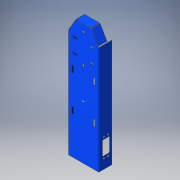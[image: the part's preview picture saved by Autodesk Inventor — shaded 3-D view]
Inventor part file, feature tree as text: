
AUTODESK INVENTOR PART (.ipt)
format: ipt  version: 2016 (Build 200138000, 138)  size: 470,016 bytes
history: native  units: in
note: dims shown in document units (in); Inventor stores cm internally (conversion verified against a paired STEP export)
features: sketch x9, other x9, sheet_metal_op x7, mirror x2, plane x1
ambient origin geometry x8: Origin, YZ Plane, XZ Plane, XY Plane, X Axis, Y Axis, Z Axis, Center Point
bodies: Solid1 (feature_tree)
feature tree (28):
  sheet_metal_op  "Face1"
  sheet_metal_op  "Flange1"
  sheet_metal_op  "Flange2"
  mirror  "Mirror2"
  plane  "Work Plane5"
  mirror  "Mirror4"
  sketch  "Sketch15"  dims[d10=0.0344in d11=0.0in d12=0.0344in d13=0.0172in d14=0.0688in d15=0.0344in d16=1.5in d17=90.0deg d18=0.0344in d19=0.1376in d20=0.0344in d21=0.0344in d22=0.0344in d23=0.0172in d24=0.0688in d25=0.0344in d26=1.0in d27=90.0deg d28=0.0344in d29=0.1376in d30=0.0344in d31=0.0344in d32=0.0344in d33=0.0in d34=0.7874in d36=4.0in d37=0.3937in d39=1.0in d41=0.0344in d42=0.0in d59=-1.375in d65=0.5in d66=0.0344in d67=0.0in d75=1.6in d76=0.8in d77=0.0676in d78=0.0676in d79=0.0676in d80=0.0676in d82=90.0deg d83=90.0deg d84=90.0deg d85=90.0deg]
  sketch  "Sketch1"  dims[d2=3.4in]
  other  "Plate1"
  sketch  "Sketch2"  dims[d3=12.0in]
  sketch  "Sketch3"  dims[d4=1.1875in]
  sketch  "Sketch4"  dims[d5=0.0344in]
  other  "Plate2"
  sheet_metal_op  "Bend1"
  sheet_metal_op  "Corner1"
  sketch  "Sketch5"  dims[d6=0.235in]
  other  "Plate3"
  sheet_metal_op  "Bend2"
  sheet_metal_op  "Corner2"
  sketch  "Sketch6"  dims[d7=0.0344in]
  sketch  "Sketch7"  dims[d8=0.0in]
  sketch  "Sketch10"  dims[d9=0.237in]
  other  "Cut1"
  other  "Cut2"
  other  "Cut3"
  other  "Cut4"
  other  "Cut6"
  other  "Definition1"
